# Revit family: Electric_Furnace-Unico-Round_Plenum
name_source: partatom
category: Mechanical Equipment
units: mm (PartAtom-declared; Revit-internal decimal feet)

## family parameters
Always vertical = Yes
Classification = None
Cut with Voids When Loaded = No
OmniClass Number = 23.75.70.00
OmniClass Title = HVAC Distribution Devices
Part Type = Normal
Room Calculation Point = No
Round Connector Dimension = Use Diameter
Shared = No
Work Plane-Based = No

## types (10) — shared parameters
Assembly Code = D3040100
Default Elevation = 0' - 0"
Description = Electric Furnace
Finish = Metal - Unico - Silver
Frequency = 60 Hz
Height = 1' - 0"
Instruction Sheet Link = https://www.unicosystem.com
Keynote = 23 30 00
Load Classification = HVAC
Manufacturer = Unico, Inc.
Manufacturer Fax Number = 314-457-9000
Performance URL = https://www.unicosystem.com
Power Factor = 1
Product Documentation Link = https://shop.unicosystem.com
Product Page URL = https://shop.unicosystem.com
URL = https://www.unicosystem.com
Version = 2020 - v1.0a
Video Link = https://www.youtube.com
Warranty URL = https://www.unicosystem.com
Width = 1' - 0"

## per-type parameters (varying)
| type | Apparent Load | Constraints | Length | Nominal Capacity | Number of Poles |
| WON0202-C | 8 VA | 1 | 1' - 1" | 2000 W | 1 |
| WON0502-C | 20 VA | 2 | 1' - 1" | 5000 W | 1 |
| WON0752-C | 31 VA | 3 | 1' - 4" | 5000 W | 1 |
| WON1002-C | 40 VA | 4 | 1' - 4" | 7500 W | 1 |
| WON1502-C | 60 VA | 5 | 1' - 9" | 7500 W | 1 |
| WON2002-C | 80 VA | 6 | 2' - 0" | 10000 W | 1 |
| WON0504-C | 12 VA | 7 | 1' - 9" | 10000 W | 3 |
| WON0754-C | 18 VA | 8 | 1' - 9" | 15000 W | 3 |
| WON1004-C | 23 VA | 9 | 1' - 9" | 15000 W | 3 |
| WON1504-C | 35 VA | 10 | 1' - 9" | 20000 W | 3 |

note: column(s) folded — value = type name in every type: Model

## geometry (parser evidence)
native form markers: Sweep x5
no freeform markers — native parametric forms only
